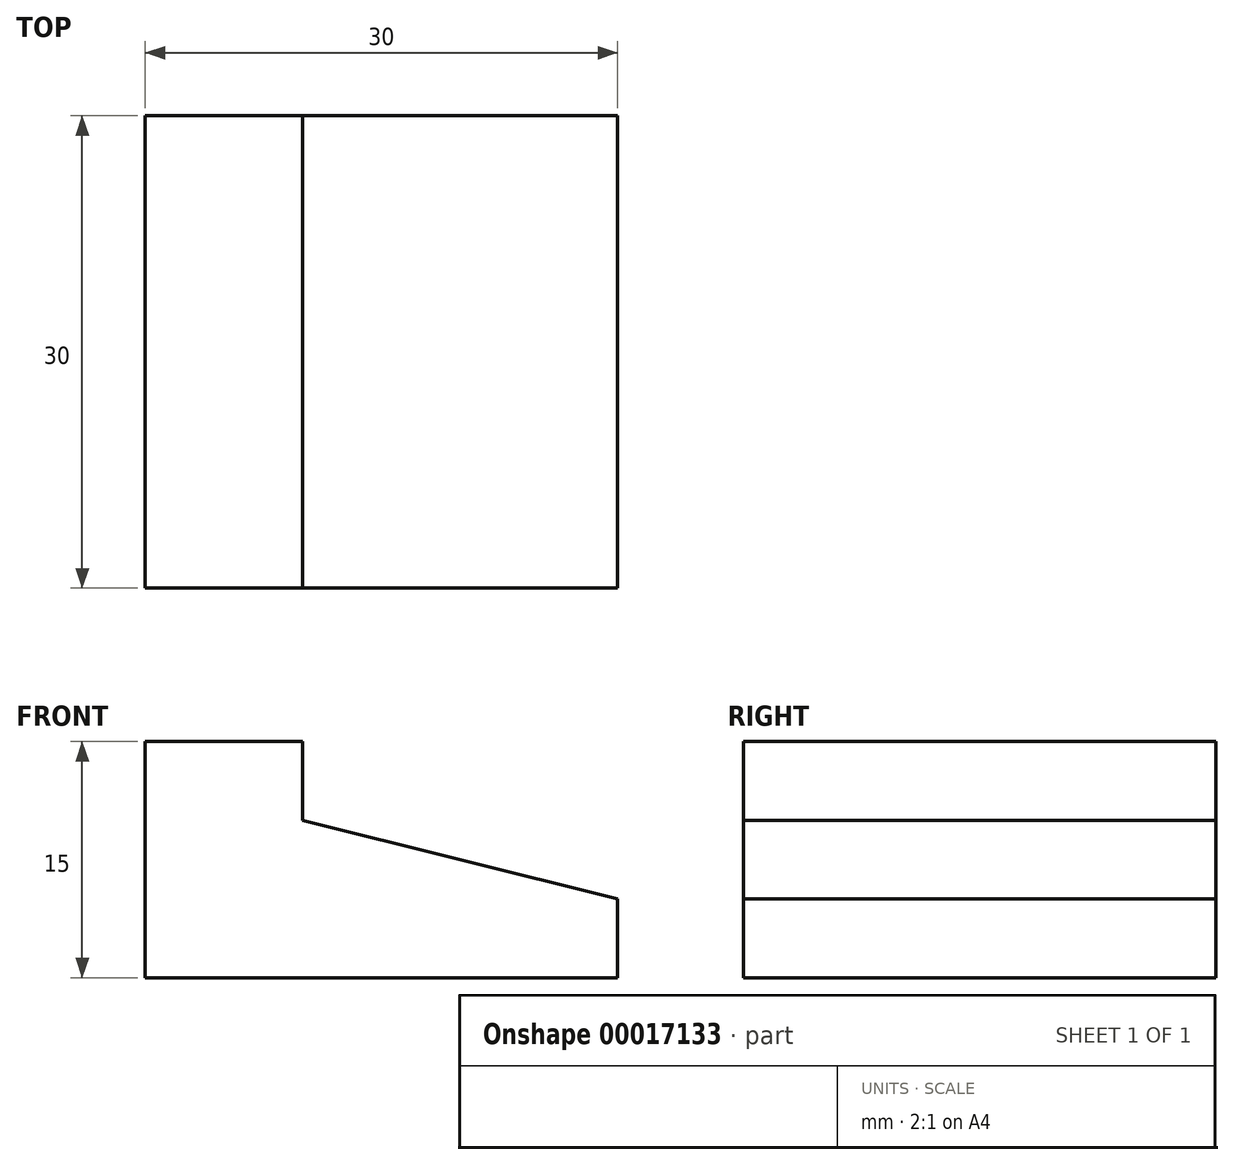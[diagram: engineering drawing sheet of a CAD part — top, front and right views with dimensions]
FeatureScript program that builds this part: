
annotation { "Feature Type Name" : "Feature", "Feature Type Description" : "" }
export const myFeature = defineFeature(function(context is Context, id is Id, definition is map)
    precondition{}
    {
        {
            var Q0;
            Q0=qCreatedBy(makeId("Front.planeOp"),FACE);
            var sketch = newSketch(context, id + "F0", { "sketchPlane" : qUnion([Q0])});
            skLineSegment(sketch, "E0", {"start": v(-19, 12.3) * mm, "end": v(-19, -2.7) * mm});
            skLineSegment(sketch, "E1", {"start": v(-19, -2.7) * mm, "end": v(11, -2.7) * mm});
            skLineSegment(sketch, "E2", {"start": v(11, -2.7) * mm, "end": v(11, 2.3) * mm});
            skLineSegment(sketch, "E3", {"start": v(11, 2.3) * mm, "end": v(-9, 7.3) * mm});
            skLineSegment(sketch, "E4", {"start": v(-9, 7.3) * mm, "end": v(-9, 12.3) * mm});
            skLineSegment(sketch, "E5", {"start": v(-9, 12.3) * mm, "end": v(-19, 12.3) * mm});
            skSolve(sketch);
        }
        {
            var Q0;
            Q0=makeQuery(id+"F0.imprint","IMPRINT",FACE,{"disambiguationData":[TD([[makeQuery(id+"F0.imprint","IMPRINT",EDGE,{"derivedFrom":sQuery(id+"F0.wireOp",EDGE,"E0")}),1.0]])]});
            extrude(context, id + "F1", {"entities" : qUnion([Q0]), "depth" : 30 * mm});
        }
    });
